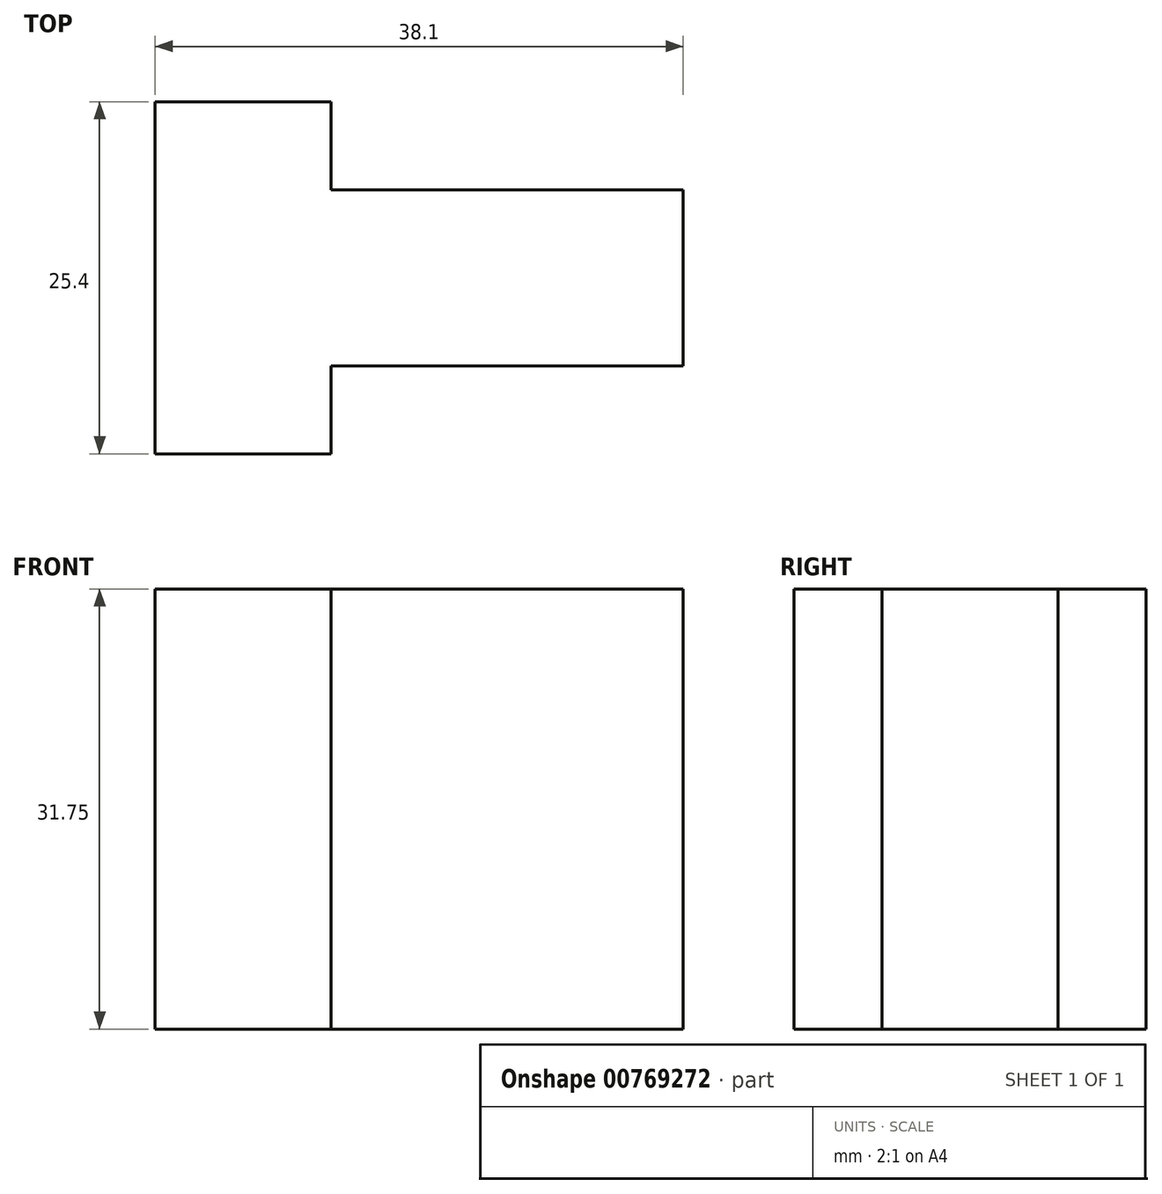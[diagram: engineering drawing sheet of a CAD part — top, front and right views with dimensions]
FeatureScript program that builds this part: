
annotation { "Feature Type Name" : "Feature", "Feature Type Description" : "" }
export const myFeature = defineFeature(function(context is Context, id is Id, definition is map)
    precondition{}
    {
        {
            var Q0;
            Q0=qCreatedBy(makeId("Top.planeOp"),FACE);
            var sketch = newSketch(context, id + "F0", { "sketchPlane" : qUnion([Q0])});
            skLineSegment(sketch, "E0", {"start": v(0, 0) * mm, "end": v(25.4, 0) * mm});
            skLineSegment(sketch, "E1", {"start": v(25.4, 0) * mm, "end": v(25.4, 12.7) * mm});
            skLineSegment(sketch, "E2", {"start": v(25.4, 12.7) * mm, "end": v(0, 12.7) * mm});
            skLineSegment(sketch, "E3", {"start": v(0, 12.7) * mm, "end": v(0, 19.05) * mm});
            skLineSegment(sketch, "E4", {"start": v(0, 19.05) * mm, "end": v(-12.7, 19.05) * mm});
            skLineSegment(sketch, "E5", {"start": v(-12.7, 19.05) * mm, "end": v(-12.7, -6.35) * mm});
            skLineSegment(sketch, "E6", {"start": v(-12.7, -6.35) * mm, "end": v(0, -6.35) * mm});
            skLineSegment(sketch, "E7", {"start": v(0, -6.35) * mm, "end": v(0, 0) * mm});
            skSolve(sketch);
        }
        {
            var Q0;
            Q0=makeQuery(id+"F0.imprint","IMPRINT",FACE,{"disambiguationData":[TD([[makeQuery(id+"F0.imprint","IMPRINT",EDGE,{"derivedFrom":sQuery(id+"F0.wireOp",EDGE,"E0")}),1.0]])]});
            extrude(context, id + "F1", {"entities" : qUnion([Q0]), "depth" : 31.75 * mm, "offsetDistance" : 25.4 * mm});
        }
    });
